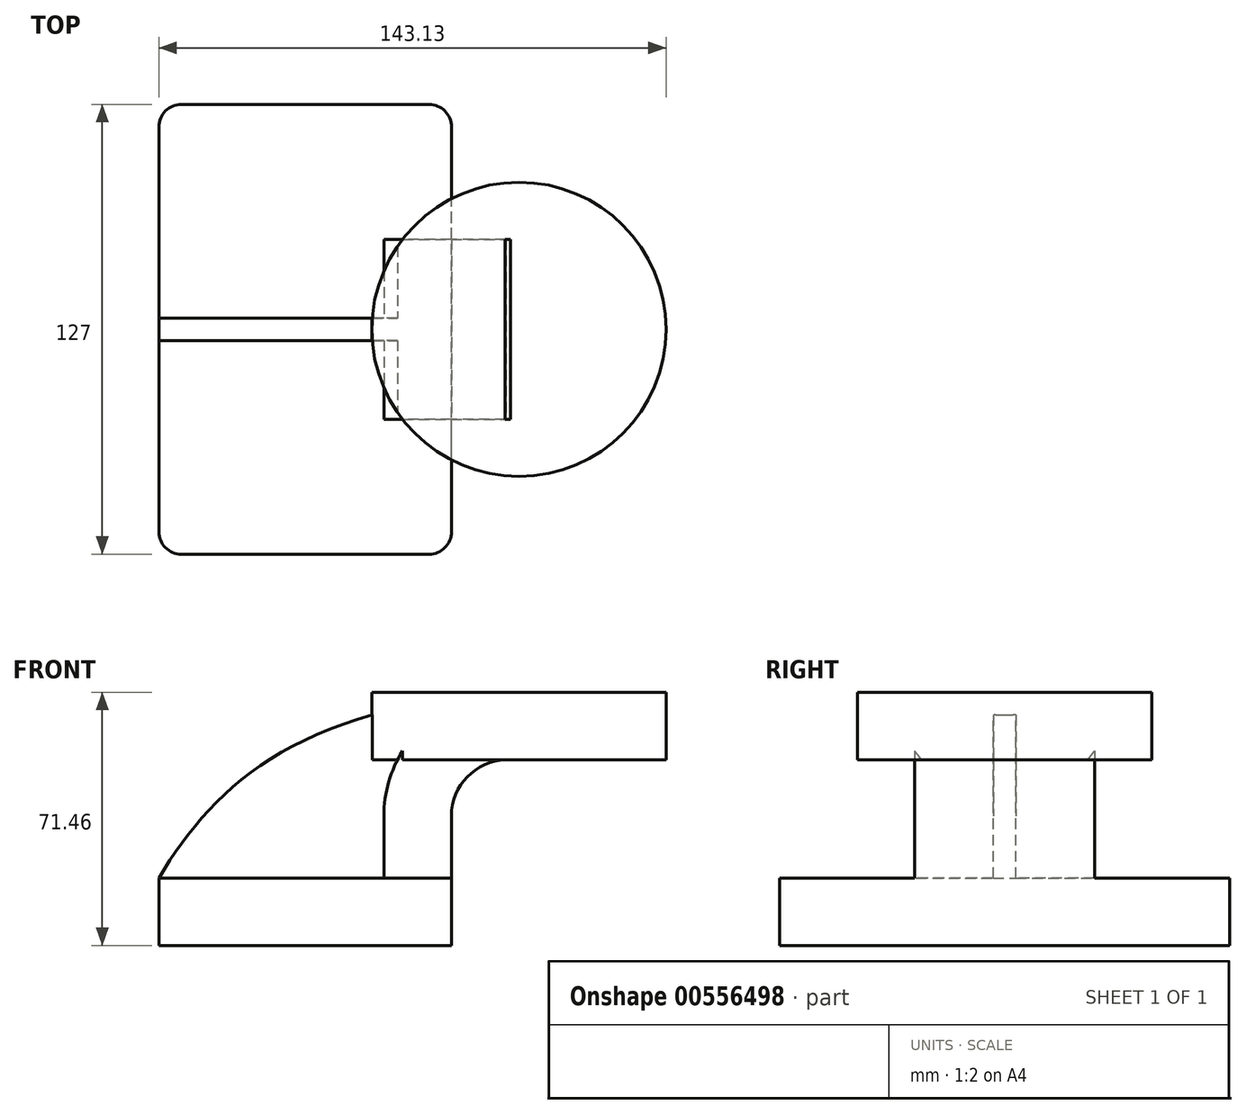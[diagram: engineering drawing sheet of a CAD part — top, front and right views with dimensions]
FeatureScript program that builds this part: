
annotation { "Feature Type Name" : "Feature", "Feature Type Description" : "" }
export const myFeature = defineFeature(function(context is Context, id is Id, definition is map)
    precondition{}
    {
        {
            var Q0;
            Q0=qCreatedBy(makeId("Front.planeOp"),FACE);
            var sketch = newSketch(context, id + "F0", { "sketchPlane" : qUnion([Q0])});
            skLineSegment(sketch, "E0.bottom", {"start": v(41.28, -9.52) * mm, "end": v(-41.28, -9.53) * mm});
            skLineSegment(sketch, "E0.top", {"start": v(41.28, 9.53) * mm, "end": v(-41.28, 9.53) * mm});
            skLineSegment(sketch, "E0.left", {"start": v(41.28, -9.52) * mm, "end": v(41.28, 9.53) * mm});
            skLineSegment(sketch, "E0.right", {"start": v(-41.28, -9.52) * mm, "end": v(-41.28, 9.53) * mm});
            skPoint(sketch, "E0.middle", {"position": v(0, 0) * mm});
            skLineSegment(sketch, "E1.bottom", {"start": v(60.32, 38.1) * mm, "end": v(111.12, 38.1) * mm});
            skLineSegment(sketch, "E1.top", {"start": v(60.32, 66.68) * mm, "end": v(111.12, 66.68) * mm});
            skLineSegment(sketch, "E1.left", {"start": v(60.32, 38.1) * mm, "end": v(60.32, 66.67) * mm});
            skLineSegment(sketch, "E1.right", {"start": v(111.12, 38.1) * mm, "end": v(111.12, 66.68) * mm});
            skPoint(sketch, "E1.middle", {"position": v(85.72, 52.39) * mm});
            skLineSegment(sketch, "E2", {"start": v(41.28, 9.53) * mm, "end": v(41.28, 27) * mm});
            skArc(sketch, "E3", {"start": v(41.27, 27) * mm, "mid": v(46.1, 38.4) * mm, "end": v(57.65, 42.88) * mm});
            skLineSegment(sketch, "E4", {"start": v(57.65, 42.88) * mm, "end": v(101.85, 42.88) * mm});
            skLineSegment(sketch, "E5.0", {"start": v(57.9, 61.93) * mm, "end": v(101.85, 61.93) * mm});
            skArc(sketch, "E5.1", {"start": v(22.23, 27) * mm, "mid": v(32.72, 51.97) * mm, "end": v(57.9, 61.93) * mm});
            skLineSegment(sketch, "E5.2", {"start": v(22.22, 9.53) * mm, "end": v(22.22, 27) * mm});
            skLineSegment(sketch, "E6", {"start": v(101.85, 38.1) * mm, "end": v(101.85, 66.68) * mm});
            skFitSpline(sketch, "E7", {"points": [v(-41.28, 9.52) * mm, v(49.11, 61) * mm], "startDerivative": vector(44.15, 73) * mm, "endDerivative": vector(164.17, 16.63) * mm});
            skSolve(sketch);
        }
        {
            var Q0;
            Q0=makeQuery(id+"F0.imprint","IMPRINT",FACE,{"disambiguationData":[TD([[makeQuery(id+"F0.imprint","IMPRINT",EDGE,{"derivedFrom":sQuery(id+"F0.wireOp",EDGE,"E0.bottom")}),-1.0]])]});
            extrude(context, id + "F1", {"entities" : qUnion([Q0]), "endBound" : BoundingType.SYMMETRIC, "depth" : 127 * mm, "offsetDistance" : 25.4 * mm});
        }
        {
            var Q0;
            {var subQ1=sQuery(id+"F0.wireOp",EDGE,"E2");Q0=makeQuery(id+"F0.imprint","IMPRINT",FACE,{"disambiguationData":[TD([[makeQuery(id+"F0.imprint","IMPRINT",EDGE,{"derivedFrom":subQ1}),1.0]])]});}
            extrude(context, id + "F2", {"entities" : qUnion([Q0]), "operationType" : NewBodyOperationType.ADD, "endBound" : BoundingType.SYMMETRIC, "oppositeDirection" : true, "depth" : 50.8 * mm, "offsetDistance" : 25.4 * mm});
        }
        {
            var Q0;
            {var subQ2=sQuery(id+"F0.wireOp",EDGE,"E5.2");Q0=makeQuery(id+"F0.imprint","IMPRINT",FACE,{"disambiguationData":[TD([[makeQuery(id+"F0.imprint","IMPRINT",EDGE,{"derivedFrom":subQ2}),1.0]])]});}
            extrude(context, id + "F3", {"entities" : qUnion([Q0]), "operationType" : NewBodyOperationType.ADD, "endBound" : BoundingType.SYMMETRIC, "depth" : 6.35 * mm, "offsetDistance" : 25.4 * mm});
        }
        {
            var Q0;
            {var subQ0=sQuery(id+"F0.wireOp",EDGE,"E4");var subQ1=sQuery(id+"F0.wireOp",EDGE,"E1.left");var subQ2=makeQuery(id+"F0.imprint","INTERSECT",VERTEX,{"derivedFrom":[subQ1,subQ0]});Q0=makeQuery(id+"F0.imprint","IMPRINT",FACE,{"disambiguationData":[TD([[makeQuery(id+"F0.imprint","IMPRINT",EDGE,{"disambiguationData":[TD([[subQ2,-1.0]])],"derivedFrom":subQ1}),-1.0]])]});}
            var Q1;
            Q1=sQuery(id+"F0.wireOp",EDGE,"E1.left");
            revolve(context, id + "F4", {"operationType" : NewBodyOperationType.ADD, "entities" : qUnion([Q0]), "axis" : qUnion([Q1]), "revolveType" : RevolveType.FULL});
        }
        {
            var Q0;
            Q0=makeQuery(id+"F1.opExtrude","CAP_EDGE",EDGE,{"disambiguationData":[OSD([sQuery(id+"F0.wireOp",EDGE,"E0.left")])],"isStart":false});
            var Q1;
            Q1=makeQuery(id+"F1.opExtrude","CAP_EDGE",EDGE,{"disambiguationData":[OSD([sQuery(id+"F0.wireOp",EDGE,"E0.right")])],"isStart":false});
            var Q2;
            Q2=makeQuery(id+"F1.opExtrude","CAP_EDGE",EDGE,{"disambiguationData":[OSD([sQuery(id+"F0.wireOp",EDGE,"E0.right")])],"isStart":true});
            var Q3;
            Q3=makeQuery(id+"F1.opExtrude","CAP_EDGE",EDGE,{"disambiguationData":[OSD([sQuery(id+"F0.wireOp",EDGE,"E0.left")])],"isStart":true});
            fillet(context, id + "F5", {"entities" : qUnion([Q0, Q1, Q2, Q3]), "radius" : 6.35 * mm, "tangentPropagation" : true, "allowEdgeOverflow" : false});
        }
    });
